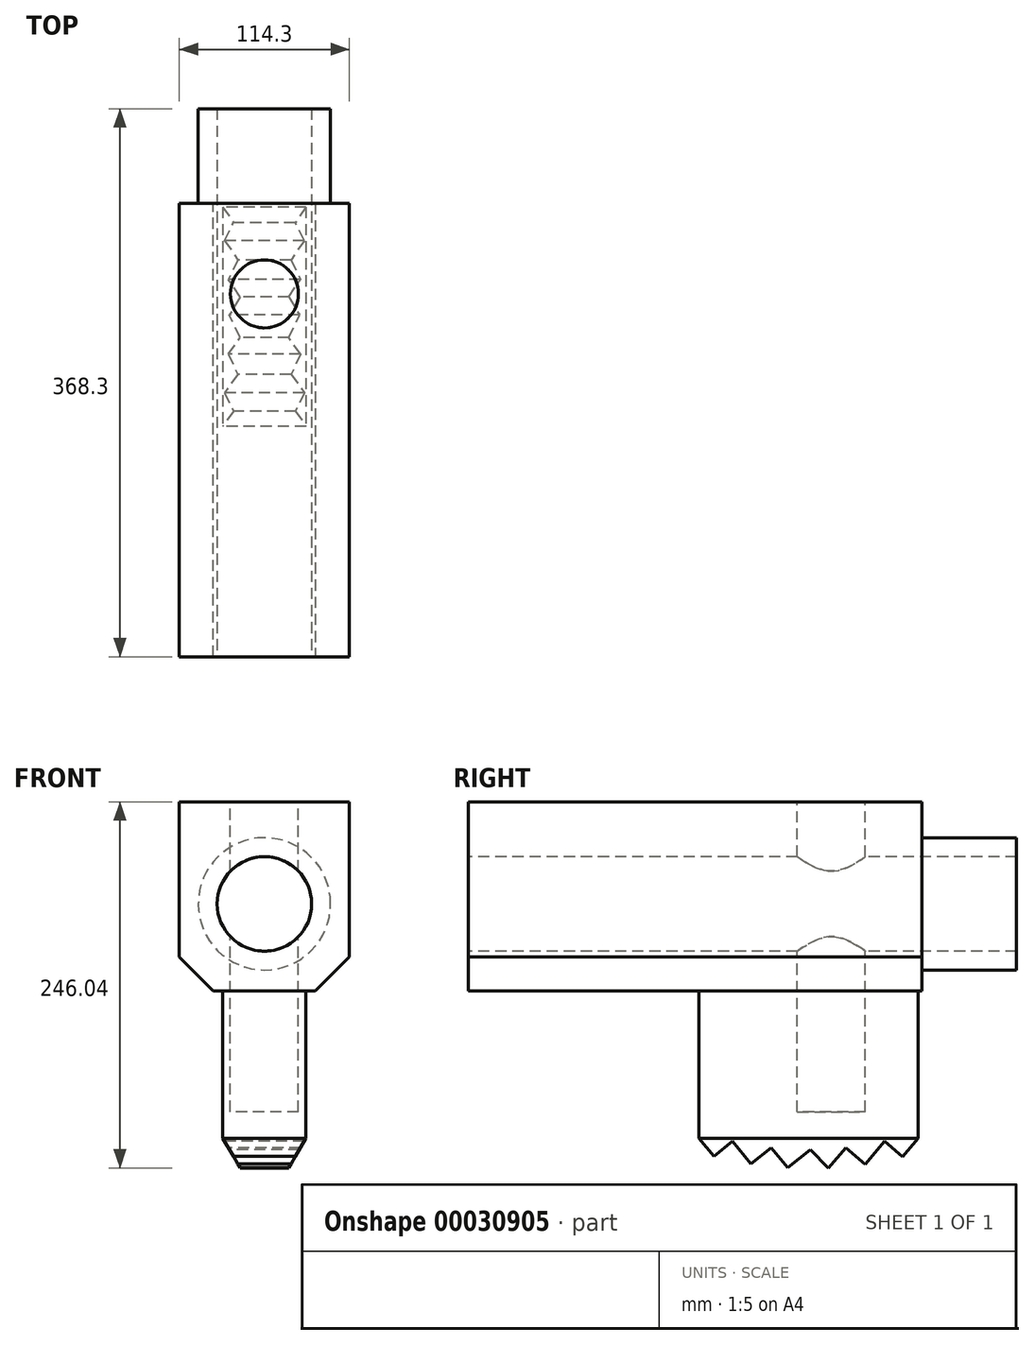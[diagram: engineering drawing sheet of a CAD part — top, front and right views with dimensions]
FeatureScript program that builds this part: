
annotation { "Feature Type Name" : "Feature", "Feature Type Description" : "" }
export const myFeature = defineFeature(function(context is Context, id is Id, definition is map)
    precondition{}
    {
        {
            var Q0;
            Q0=qCreatedBy(makeId("Front.planeOp"),FACE);
            var sketch = newSketch(context, id + "F0", { "sketchPlane" : qUnion([Q0])});
            skLineSegment(sketch, "E0.rect.bottom", {"start": v(57.15, -63.5) * mm, "end": v(-57.15, -63.5) * mm});
            skLineSegment(sketch, "E0.rect.top", {"start": v(57.15, 63.5) * mm, "end": v(-57.15, 63.5) * mm});
            skLineSegment(sketch, "E0.rect.left", {"start": v(57.15, -63.5) * mm, "end": v(57.15, 63.5) * mm});
            skLineSegment(sketch, "E0.rect.right", {"start": v(-57.15, -63.5) * mm, "end": v(-57.15, 63.5) * mm});
            skPoint(sketch, "E0.rect.middle", {"position": v(0, 0) * mm});
            skSolve(sketch);
        }
        {
            var Q0;
            Q0=makeQuery(id+"F0.imprint","IMPRINT",FACE,{"disambiguationData":[TD([[makeQuery(id+"F0.imprint","IMPRINT",EDGE,{"derivedFrom":sQuery(id+"F0.wireOp",EDGE,"E0.rect.bottom")}),-1.0]])]});
            extrude(context, id + "F1", {"entities" : qUnion([Q0]), "oppositeDirection" : true, "depth" : 304.8 * mm});
        }
        {
            var Q0;
            Q0=makeQuery(id+"F1.opExtrude","SWEPT_EDGE",EDGE,{"disambiguationData":[OSD([sQuery(id+"F0.wireOp",EDGE,"E0.rect.bottom"),sQuery(id+"F0.wireOp",EDGE,"E0.rect.left")])]});
            var Q1;
            Q1=makeQuery(id+"F1.opExtrude","SWEPT_EDGE",EDGE,{"disambiguationData":[OSD([sQuery(id+"F0.wireOp",EDGE,"E0.rect.bottom"),sQuery(id+"F0.wireOp",EDGE,"E0.rect.right")])]});
            chamfer(context, id + "F2", {"entities" : qUnion([Q0, Q1]), "chamferType" : ChamferType.OFFSET_ANGLE, "width" : 22.86 * mm, "oppositeDirection" : false, "angle" : 45 * degree, "tangentPropagation" : true});
        }
        {
            var Q0;
            Q0=makeQuery(id+"F1.opExtrude","CAP_FACE",FACE,{"disambiguationData":[OSD([sQuery(id+"F0.wireOp",EDGE,"E0.rect.bottom"),sQuery(id+"F0.wireOp",EDGE,"E0.rect.top"),sQuery(id+"F0.wireOp",EDGE,"E0.rect.left"),sQuery(id+"F0.wireOp",EDGE,"E0.rect.right")])],"isStart":true});
            var sketch = newSketch(context, id + "F3", { "sketchPlane" : qUnion([Q0])});
            skCircle(sketch, "E1", {"center": v(0, -5.08) * mm, "radius": 31.75 * mm});
            skSolve(sketch);
        }
        {
            var Q0;
            Q0=sQuery(id+"F3.wireOp",VERTEX,"E1.center");
            var Q1;
            Q1=makeQuery(id+"F1.opExtrude","SWEPT_BODY",BODY,{"disambiguationData":[OSD([sQuery(id+"F0.wireOp",EDGE,"E0.rect.bottom"),sQuery(id+"F0.wireOp",EDGE,"E0.rect.top"),sQuery(id+"F0.wireOp",EDGE,"E0.rect.left"),sQuery(id+"F0.wireOp",EDGE,"E0.rect.right")])]});
            hole(context, id + "F4", {"style" : HoleStyle.SIMPLE, "holeDiameter" : 63.5 * mm, "endStyle" : HoleEndStyle.THROUGH, "locations" : qUnion([Q0]), "scope" : qUnion([Q1])});
        }
        {
            var Q0;
            Q0=makeQuery(id+"F1.opExtrude","CAP_FACE",FACE,{"disambiguationData":[OSD([sQuery(id+"F0.wireOp",EDGE,"E0.rect.bottom"),sQuery(id+"F0.wireOp",EDGE,"E0.rect.top"),sQuery(id+"F0.wireOp",EDGE,"E0.rect.left"),sQuery(id+"F0.wireOp",EDGE,"E0.rect.right")])],"isStart":false});
            var sketch = newSketch(context, id + "F5", { "sketchPlane" : qUnion([Q0])});
            skCircle(sketch, "E2", {"center": v(0, -5.08) * mm, "radius": 44.45 * mm});
            skSolve(sketch);
        }
        {
            var Q0;
            Q0=makeQuery(id+"F5.imprint","IMPRINT",FACE,{"disambiguationData":[TD([[makeQuery(id+"F5.imprint","IMPRINT",EDGE,{"derivedFrom":sQuery(id+"F5.wireOp",EDGE,"E2")}),1.0]])]});
            extrude(context, id + "F6", {"entities" : qUnion([Q0]), "operationType" : NewBodyOperationType.ADD, "depth" : 63.5 * mm});
        }
        {
            var Q0;
            Q0=makeQuery(id+"F1.opExtrude","CAP_FACE",FACE,{"disambiguationData":[OSD([sQuery(id+"F0.wireOp",EDGE,"E0.rect.bottom"),sQuery(id+"F0.wireOp",EDGE,"E0.rect.top"),sQuery(id+"F0.wireOp",EDGE,"E0.rect.left"),sQuery(id+"F0.wireOp",EDGE,"E0.rect.right")])],"isStart":true});
            cPlane(context, id + "F7", {"entities" : qUnion([Q0]), "cplaneType" : CPlaneType.OFFSET, "offset" : 154.94 * mm, "oppositeDirection" : true, "width" : 152.4 * mm, "height" : 152.4 * mm});
        }
        {
            var Q0;
            Q0=qCreatedBy(id+"F7.planeOp",FACE);
            var sketch = newSketch(context, id + "F8", { "sketchPlane" : qUnion([Q0])});
            skLineSegment(sketch, "E3.bottom", {"start": v(-27.94, -63.5) * mm, "end": v(27.94, -63.5) * mm});
            skLineSegment(sketch, "E3.top", {"start": v(-27.94, -162.56) * mm, "end": v(27.94, -162.56) * mm});
            skLineSegment(sketch, "E3.left", {"start": v(-27.94, -63.5) * mm, "end": v(-27.94, -162.56) * mm});
            skLineSegment(sketch, "E3.right", {"start": v(27.94, -63.5) * mm, "end": v(27.94, -162.56) * mm});
            skSolve(sketch);
        }
        {
            var Q0;
            Q0=makeQuery(id+"F8.imprint","IMPRINT",FACE,{"disambiguationData":[TD([[makeQuery(id+"F8.imprint","IMPRINT",EDGE,{"derivedFrom":sQuery(id+"F8.wireOp",EDGE,"E3.bottom")}),-1.0]])]});
            extrude(context, id + "F9", {"entities" : qUnion([Q0]), "operationType" : NewBodyOperationType.ADD, "oppositeDirection" : true, "depth" : 147.32 * mm});
        }
        {
            var Q0;
            Q0=makeQuery(id+"F9.opExtrude","SWEPT_FACE",FACE,{"disambiguationData":[OSD([sQuery(id+"F8.wireOp",EDGE,"E3.left")])]});
            var sketch = newSketch(context, id + "F10", { "sketchPlane" : qUnion([Q0])});
            skCircle(sketch, "E4", {"center": v(-228.6, 71.12) * mm, "radius": 254 * mm, "construction": true});
            skLineSegment(sketch, "E5", {"start": v(-357.99, -182.88) * mm, "end": v(-95.1, -182.88) * mm, "construction": true});
            skLineSegment(sketch, "E6", {"start": v(-228.6, 71.12) * mm, "end": v(-199.4, -206.69) * mm, "construction": true});
            skLineSegment(sketch, "E7", {"start": v(-228.6, 71.12) * mm, "end": v(-228.6, 130.32) * mm, "construction": true});
            skCircle(sketch, "E8", {"center": v(-228.6, 71.12) * mm, "radius": 241.3 * mm, "construction": true});
            skLineSegment(sketch, "E9", {"start": v(-203.38, -168.86) * mm, "end": v(-214.41, -182.48) * mm});
            skLineSegment(sketch, "E10", {"start": v(-203.38, -168.86) * mm, "end": v(-189.75, -179.9) * mm});
            skLineSegment(sketch, "E11", {"start": v(-189.75, -179.9) * mm, "end": v(-177.45, -164.7) * mm});
            skLineSegment(sketch, "E12", {"start": v(-177.45, -164.7) * mm, "end": v(-164.9, -174.86) * mm});
            skLineSegment(sketch, "E13", {"start": v(-164.9, -174.86) * mm, "end": v(-154.94, -162.56) * mm});
            skLineSegment(sketch, "E14", {"start": v(-214.41, -182.48) * mm, "end": v(-229.6, -170.18) * mm});
            skLineSegment(sketch, "E15", {"start": v(-279.71, -164.7) * mm, "end": v(-291.61, -174.94) * mm});
            skLineSegment(sketch, "E16", {"start": v(-302.26, -162.56) * mm, "end": v(-291.61, -174.94) * mm});
            skLineSegment(sketch, "E17", {"start": v(-279.71, -164.7) * mm, "end": v(-266.53, -180.03) * mm});
            skLineSegment(sketch, "E18", {"start": v(-266.53, -180.03) * mm, "end": v(-253.57, -168.88) * mm});
            skLineSegment(sketch, "E19", {"start": v(-241.83, -182.54) * mm, "end": v(-253.57, -168.88) * mm});
            skLineSegment(sketch, "E20", {"start": v(-241.83, -182.54) * mm, "end": v(-229.6, -170.18) * mm});
            skLineSegment(sketch, "E21", {"start": v(-302.26, -162.56) * mm, "end": v(-154.94, -162.56) * mm});
            skSolve(sketch);
        }
        {
            var Q0;
            Q0=makeQuery(id+"F10.imprint","IMPRINT",FACE,{"disambiguationData":[TD([[makeQuery(id+"F10.imprint","IMPRINT",EDGE,{"derivedFrom":sQuery(id+"F10.wireOp",EDGE,"E9")}),-1.0]])]});
            extrude(context, id + "F11", {"entities" : qUnion([Q0]), "oppositeDirection" : true, "depth" : 55.88 * mm});
        }
        {
            var Q0;
            Q0=makeQuery(id+"F9.opExtrude","CAP_FACE",FACE,{"disambiguationData":[OSD([sQuery(id+"F8.wireOp",EDGE,"E3.bottom"),sQuery(id+"F8.wireOp",EDGE,"E3.top"),sQuery(id+"F8.wireOp",EDGE,"E3.left"),sQuery(id+"F8.wireOp",EDGE,"E3.right")])],"isStart":false});
            var sketch = newSketch(context, id + "F12", { "sketchPlane" : qUnion([Q0])});
            skLineSegment(sketch, "E22", {"start": v(-27.94, -162.56) * mm, "end": v(-13.85, -186.96) * mm});
            skLineSegment(sketch, "E23", {"start": v(-13.85, -186.96) * mm, "end": v(-27.94, -186.96) * mm});
            skLineSegment(sketch, "E24", {"start": v(-27.94, -186.96) * mm, "end": v(-27.94, -162.56) * mm});
            skLineSegment(sketch, "E25", {"start": v(0, -162.56) * mm, "end": v(0, -197.08) * mm, "construction": true});
            skLineSegment(sketch, "E26.MirrorCS", {"start": v(27.94, -162.56) * mm, "end": v(13.85, -186.96) * mm});
            skLineSegment(sketch, "E27.MirrorCS", {"start": v(13.85, -186.96) * mm, "end": v(27.94, -186.96) * mm});
            skLineSegment(sketch, "E28.MirrorCS", {"start": v(27.94, -186.96) * mm, "end": v(27.94, -162.56) * mm});
            skSolve(sketch);
        }
        {
            var Q0;
            Q0=makeQuery(id+"F12.imprint","IMPRINT",FACE,{"disambiguationData":[TD([[makeQuery(id+"F12.imprint","IMPRINT",EDGE,{"derivedFrom":sQuery(id+"F12.wireOp",EDGE,"E22")}),-1.0]])]});
            var Q1;
            Q1=makeQuery(id+"F12.imprint","IMPRINT",FACE,{"disambiguationData":[TD([[makeQuery(id+"F12.imprint","IMPRINT",EDGE,{"derivedFrom":sQuery(id+"F12.wireOp",EDGE,"E26.MirrorCS")}),1.0]])]});
            extrude(context, id + "F13", {"entities" : qUnion([Q0, Q1]), "operationType" : NewBodyOperationType.REMOVE, "endBound" : BoundingType.THROUGH_ALL, "oppositeDirection" : true, "depth" : 25.4 * mm});
        }
        {
            var Q0;
            Q0=makeQuery(id+"F1.opExtrude","SWEPT_FACE",FACE,{"disambiguationData":[OSD([sQuery(id+"F0.wireOp",EDGE,"E0.rect.top")])]});
            var sketch = newSketch(context, id + "F14", { "sketchPlane" : qUnion([Q0])});
            skCircle(sketch, "E29", {"center": v(0, 243.84) * mm, "radius": 22.86 * mm});
            skSolve(sketch);
        }
        {
            var Q0;
            Q0=makeQuery(id+"F14.imprint","IMPRINT",FACE,{"disambiguationData":[TD([[makeQuery(id+"F14.imprint","IMPRINT",EDGE,{"derivedFrom":sQuery(id+"F14.wireOp",EDGE,"E29")}),1.0]])]});
            extrude(context, id + "F15", {"entities" : qUnion([Q0]), "operationType" : NewBodyOperationType.REMOVE, "oppositeDirection" : true, "depth" : 208.28 * mm});
        }
    });
